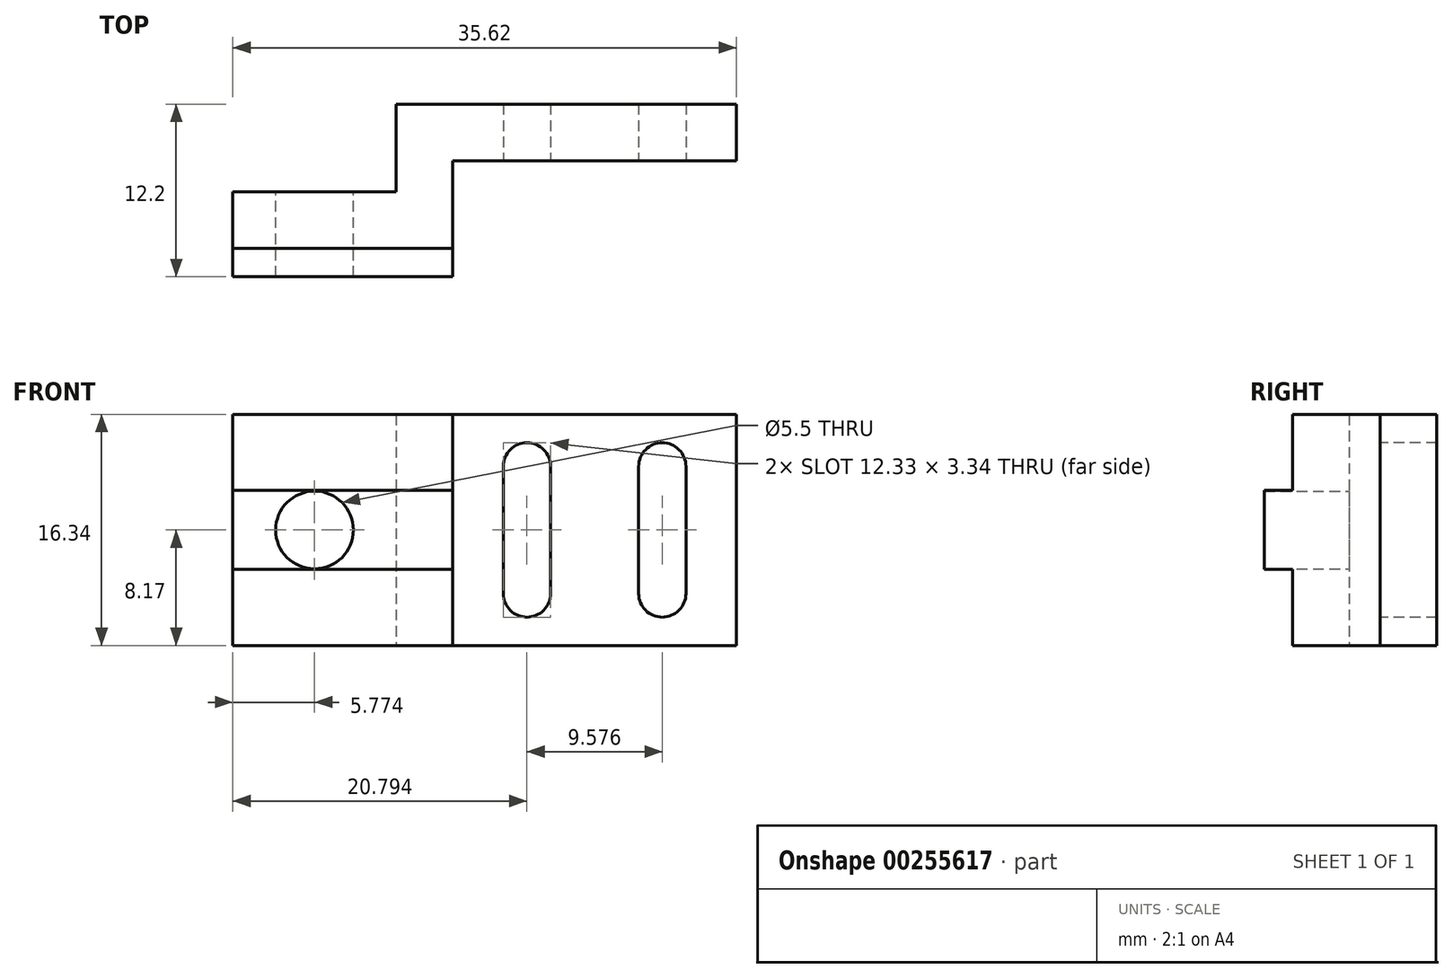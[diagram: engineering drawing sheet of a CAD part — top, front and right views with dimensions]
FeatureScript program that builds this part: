
annotation { "Feature Type Name" : "Feature", "Feature Type Description" : "" }
export const myFeature = defineFeature(function(context is Context, id is Id, definition is map)
    precondition{}
    {
        {
            var Q0;
            Q0=qCreatedBy(makeId("Top.planeOp"),FACE);
            var sketch = newSketch(context, id + "F0", { "sketchPlane" : qUnion([Q0])});
            skLineSegment(sketch, "E0.bottom", {"start": v(0, 0) * mm, "end": v(15.55, 0) * mm});
            skLineSegment(sketch, "E0.top", {"start": v(0, 4) * mm, "end": v(11.55, 4) * mm});
            skLineSegment(sketch, "E0.left", {"start": v(0, 0) * mm, "end": v(0, 4) * mm});
            skLineSegment(sketch, "E0.right", {"start": v(15.55, 0) * mm, "end": v(15.55, 6.2) * mm});
            skLineSegment(sketch, "E1.bottom", {"start": v(11.55, 10.2) * mm, "end": v(35.62, 10.2) * mm});
            skLineSegment(sketch, "E1.top", {"start": v(15.55, 6.2) * mm, "end": v(35.62, 6.2) * mm});
            skLineSegment(sketch, "E1.left", {"start": v(11.55, 10.2) * mm, "end": v(11.55, 4) * mm});
            skLineSegment(sketch, "E1.right", {"start": v(35.62, 10.2) * mm, "end": v(35.62, 6.2) * mm});
            skSolve(sketch);
        }
        {
            var Q0;
            Q0 = qSketchRegion(id + "F0", true);
            extrude(context, id + "F1", {"entities" : qUnion([Q0]), "endBound" : BoundingType.SYMMETRIC, "depth" : 16.33 * mm});
        }
        {
            var Q0;
            Q0=makeQuery(id+"F1.opExtrude","SWEPT_FACE",FACE,{"disambiguationData":[OSD([sQuery(id+"F0.wireOp",EDGE,"E0.top")])]});
            var sketch = newSketch(context, id + "F2", { "sketchPlane" : qUnion([Q0])});
            skCircle(sketch, "E2", {"center": v(-5.77, 0) * mm, "radius": 2.75 * mm});
            skPoint(sketch, "E2.centerSnap0", {"position": v(-11.55, 0) * mm});
            skLineSegment(sketch, "E3", {"start": v(-5.77, -8.17) * mm, "end": v(-5.77, 8.17) * mm, "construction": true});
            skSolve(sketch);
        }
        {
            var Q0;
            Q0 = qSketchRegion(id + "F2", true);
            extrude(context, id + "F3", {"entities" : qUnion([Q0]), "operationType" : NewBodyOperationType.REMOVE, "endBound" : BoundingType.THROUGH_ALL, "oppositeDirection" : true, "depth" : 25 * mm});
        }
        {
            var Q0;
            Q0=makeQuery(id+"F1.opExtrude","SWEPT_FACE",FACE,{"disambiguationData":[OSD([sQuery(id+"F0.wireOp",EDGE,"E1.top")])]});
            var sketch = newSketch(context, id + "F4", { "sketchPlane" : qUnion([Q0])});
            skLineSegment(sketch, "E4", {"start": v(19.12, 4.5) * mm, "end": v(19.12, -4.5) * mm});
            skLineSegment(sketch, "E5", {"start": v(22.47, 4.5) * mm, "end": v(22.47, -4.5) * mm});
            skArc(sketch, "E6", {"start": v(22.47, 4.5) * mm, "mid": v(20.8, 6.17) * mm, "end": v(19.12, 4.5) * mm});
            skArc(sketch, "E7", {"start": v(19.12, -4.5) * mm, "mid": v(20.8, -6.17) * mm, "end": v(22.47, -4.5) * mm});
            skLineSegment(sketch, "E8", {"start": v(25.58, 8.17) * mm, "end": v(25.58, -8.17) * mm, "construction": true});
            skArc(sketch, "E9.MirrorCS", {"start": v(28.7, 4.5) * mm, "mid": v(30.37, 6.17) * mm, "end": v(32.04, 4.5) * mm});
            skLineSegment(sketch, "E10.MirrorCS", {"start": v(28.7, 4.5) * mm, "end": v(28.7, -4.5) * mm});
            skArc(sketch, "E11.MirrorCS", {"start": v(32.04, -4.5) * mm, "mid": v(30.37, -6.17) * mm, "end": v(28.7, -4.5) * mm});
            skLineSegment(sketch, "E12.MirrorCS", {"start": v(32.04, 4.5) * mm, "end": v(32.04, -4.5) * mm});
            skCircle(sketch, "E13", {"center": v(20.8, 4.5) * mm, "radius": 1.44 * mm, "construction": true});
            skCircle(sketch, "E14.MirrorC", {"center": v(30.37, 4.5) * mm, "radius": 1.44 * mm, "construction": true});
            skSolve(sketch);
        }
        {
            var Q0;
            Q0 = qSketchRegion(id + "F4", true);
            extrude(context, id + "F5", {"entities" : qUnion([Q0]), "operationType" : NewBodyOperationType.REMOVE, "endBound" : BoundingType.THROUGH_ALL, "oppositeDirection" : true, "depth" : 25 * mm});
        }
        {
            var Q0;
            Q0=makeQuery(id+"F1.opExtrude","SWEPT_FACE",FACE,{"disambiguationData":[OSD([sQuery(id+"F0.wireOp",EDGE,"E0.bottom")])]});
            var sketch = newSketch(context, id + "F6", { "sketchPlane" : qUnion([Q0])});
            skLineSegment(sketch, "E15.bottom", {"start": v(0, 2.8) * mm, "end": v(15.55, 2.8) * mm});
            skLineSegment(sketch, "E15.top", {"start": v(0, -2.8) * mm, "end": v(15.55, -2.8) * mm});
            skLineSegment(sketch, "E15.left", {"start": v(0, 2.8) * mm, "end": v(0, -2.8) * mm});
            skLineSegment(sketch, "E15.right", {"start": v(15.55, 2.8) * mm, "end": v(15.55, -2.8) * mm});
            skSolve(sketch);
        }
        {
            var Q0;
            Q0=makeQuery(id+"F6.imprint","IMPRINT",FACE,{"disambiguationData":[TD([[makeQuery(id+"F6.imprint","IMPRINT",EDGE,{"derivedFrom":sQuery(id+"F6.wireOp",EDGE,"E15.bottom")}),-1.0]])]});
            extrude(context, id + "F7", {"entities" : qUnion([Q0]), "operationType" : NewBodyOperationType.ADD, "depth" : 2 * mm});
        }
    });
